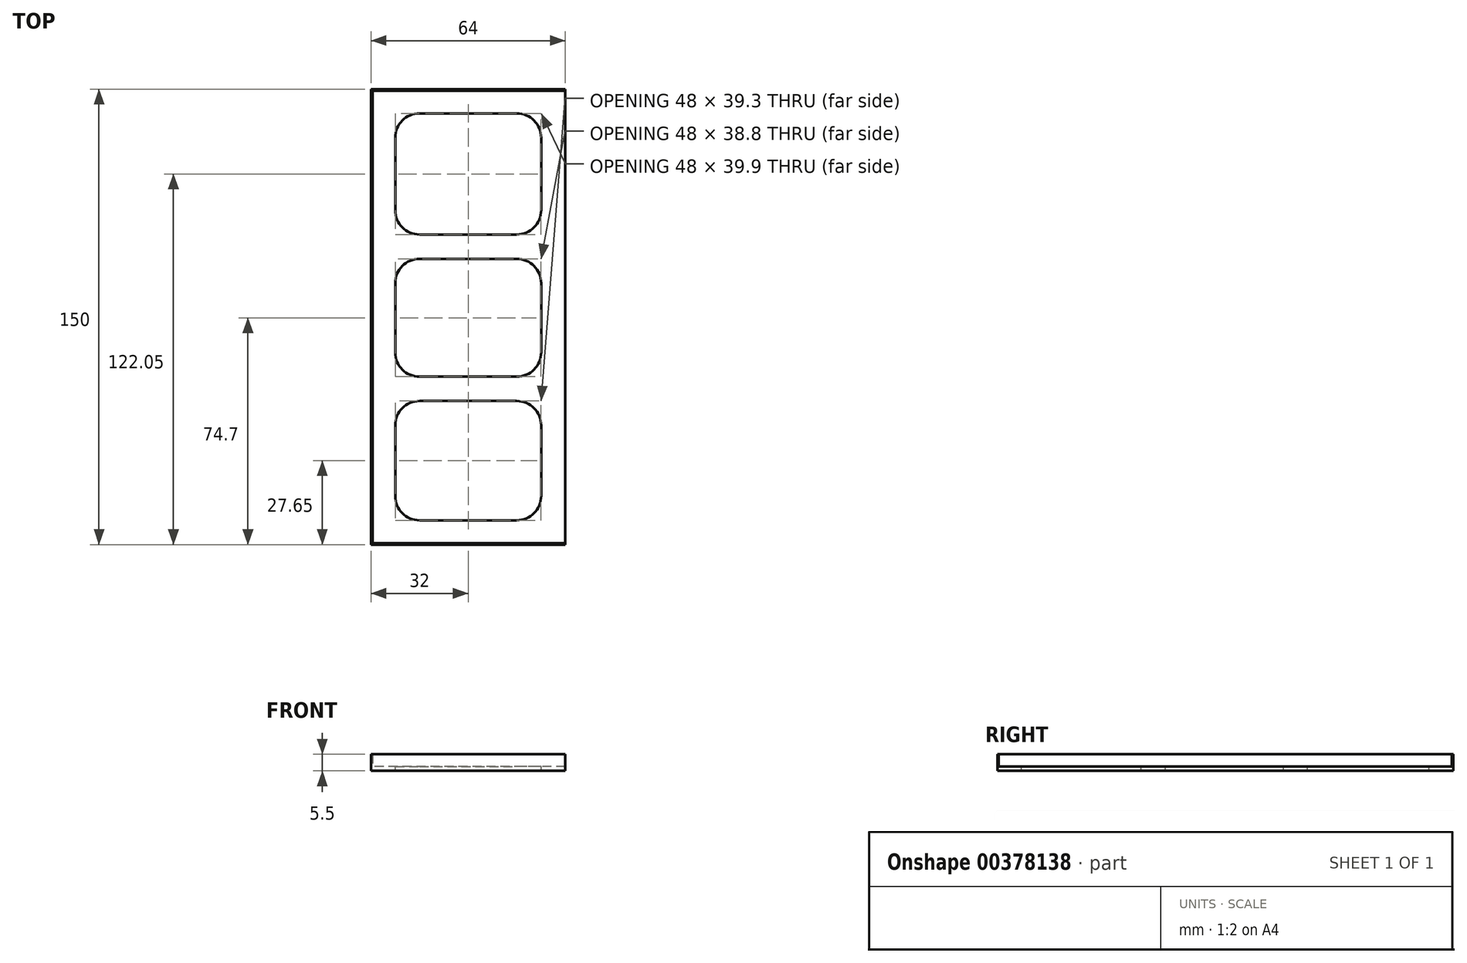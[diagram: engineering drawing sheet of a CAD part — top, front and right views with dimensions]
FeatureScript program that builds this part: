
annotation { "Feature Type Name" : "Feature", "Feature Type Description" : "" }
export const myFeature = defineFeature(function(context is Context, id is Id, definition is map)
    precondition{}
    {
        {
            var Q0;
            Q0=qCreatedBy(makeId("Top.planeOp"),FACE);
            var sketch = newSketch(context, id + "F0", { "sketchPlane" : qUnion([Q0])});
            skLineSegment(sketch, "E0.bottom", {"start": v(0, 0) * mm, "end": v(64, 0) * mm});
            skLineSegment(sketch, "E0.top", {"start": v(0, 150) * mm, "end": v(64, 150) * mm});
            skLineSegment(sketch, "E0.left", {"start": v(0, 0) * mm, "end": v(0, 150) * mm});
            skLineSegment(sketch, "E0.right", {"start": v(64, 0) * mm, "end": v(64, 150) * mm});
            skSolve(sketch);
        }
        {
            var Q0;
            Q0=qSketchRegion(id+"F0",true);
            extrude(context, id + "F1", {"entities" : qUnion([Q0]), "flatOperationType" : FlatOperationType.REMOVE, "offsetDistance" : 25 * mm, "depth" : 1.5 * mm, "domain" : OperationDomain.MODEL});
        }
        {
            var Q0;
            Q0=makeQuery(id+"F1.opExtrude","CAP_FACE",FACE,{"disambiguationData":[OSD([sQuery(id+"F0.wireOp",EDGE,"E0.bottom"),sQuery(id+"F0.wireOp",EDGE,"E0.top"),sQuery(id+"F0.wireOp",EDGE,"E0.left"),sQuery(id+"F0.wireOp",EDGE,"E0.right")])],"isStart":false});
            var sketch = newSketch(context, id + "F2", { "sketchPlane" : qUnion([Q0])});
            skLineSegment(sketch, "E1.bottom", {"start": v(8, 8) * mm, "end": v(56, 8) * mm});
            skLineSegment(sketch, "E1.top", {"start": v(8, 47.3) * mm, "end": v(56, 47.3) * mm});
            skLineSegment(sketch, "E1.left", {"start": v(8, 8) * mm, "end": v(8, 47.3) * mm});
            skLineSegment(sketch, "E1.right", {"start": v(56, 8) * mm, "end": v(56, 47.3) * mm});
            skLineSegment(sketch, "E2.bottom", {"start": v(8, 142) * mm, "end": v(56, 142) * mm});
            skLineSegment(sketch, "E2.top", {"start": v(8, 102.1) * mm, "end": v(56, 102.1) * mm});
            skLineSegment(sketch, "E2.left", {"start": v(8, 142) * mm, "end": v(8, 102.1) * mm});
            skLineSegment(sketch, "E2.right", {"start": v(56, 142) * mm, "end": v(56, 102.1) * mm});
            skLineSegment(sketch, "E3.bottom", {"start": v(8, 94.1) * mm, "end": v(56, 94.1) * mm});
            skLineSegment(sketch, "E3.top", {"start": v(8, 55.3) * mm, "end": v(56, 55.3) * mm});
            skLineSegment(sketch, "E3.left", {"start": v(8, 94.1) * mm, "end": v(8, 55.3) * mm});
            skLineSegment(sketch, "E3.right", {"start": v(56, 94.1) * mm, "end": v(56, 55.3) * mm});
            skSolve(sketch);
        }
        {
            var Q0;
            Q0=makeQuery(id+"F2.imprint","IMPRINT",FACE,{"disambiguationData":[TD([[makeQuery(id+"F2.imprint","IMPRINT",EDGE,{"derivedFrom":sQuery(id+"F2.wireOp",EDGE,"E2.bottom")}),-1.0]])]});
            var Q1;
            Q1=makeQuery(id+"F2.imprint","IMPRINT",FACE,{"disambiguationData":[TD([[makeQuery(id+"F2.imprint","IMPRINT",EDGE,{"derivedFrom":sQuery(id+"F2.wireOp",EDGE,"E3.bottom")}),-1.0]])]});
            var Q2;
            Q2=makeQuery(id+"F2.imprint","IMPRINT",FACE,{"disambiguationData":[TD([[makeQuery(id+"F2.imprint","IMPRINT",EDGE,{"derivedFrom":sQuery(id+"F2.wireOp",EDGE,"E1.bottom")}),1.0]])]});
            extrude(context, id + "F3", {"entities" : qUnion([Q0, Q1, Q2]), "operationType" : NewBodyOperationType.REMOVE, "flatOperationType" : FlatOperationType.REMOVE, "endBound" : BoundingType.THROUGH_ALL, "oppositeDirection" : true, "offsetDistance" : 25 * mm, "depth" : 25 * mm, "domain" : OperationDomain.MODEL});
        }
        {
            var Q0;
            Q0=makeQuery(id+"F3.boolean.opBoolean","COPY",EDGE,{"derivedFrom":makeQuery(id+"F3.opExtrude","SWEPT_EDGE",EDGE,{"disambiguationData":[OSD([sQuery(id+"F2.wireOp",EDGE,"E2.bottom"),sQuery(id+"F2.wireOp",EDGE,"E2.left")])]})});
            var Q1;
            Q1=makeQuery(id+"F3.boolean.opBoolean","COPY",EDGE,{"derivedFrom":makeQuery(id+"F3.opExtrude","SWEPT_EDGE",EDGE,{"disambiguationData":[OSD([sQuery(id+"F2.wireOp",EDGE,"E3.bottom"),sQuery(id+"F2.wireOp",EDGE,"E3.left")])]})});
            var Q2;
            Q2=makeQuery(id+"F3.boolean.opBoolean","COPY",EDGE,{"derivedFrom":makeQuery(id+"F3.opExtrude","SWEPT_EDGE",EDGE,{"disambiguationData":[OSD([sQuery(id+"F2.wireOp",EDGE,"E1.top"),sQuery(id+"F2.wireOp",EDGE,"E1.left")])]})});
            var Q3;
            Q3=makeQuery(id+"F3.boolean.opBoolean","COPY",EDGE,{"derivedFrom":makeQuery(id+"F3.opExtrude","SWEPT_EDGE",EDGE,{"disambiguationData":[OSD([sQuery(id+"F2.wireOp",EDGE,"E2.top"),sQuery(id+"F2.wireOp",EDGE,"E2.left")])]})});
            var Q4;
            Q4=makeQuery(id+"F3.boolean.opBoolean","COPY",EDGE,{"derivedFrom":makeQuery(id+"F3.opExtrude","SWEPT_EDGE",EDGE,{"disambiguationData":[OSD([sQuery(id+"F2.wireOp",EDGE,"E3.top"),sQuery(id+"F2.wireOp",EDGE,"E3.left")])]})});
            var Q5;
            Q5=makeQuery(id+"F3.boolean.opBoolean","COPY",EDGE,{"derivedFrom":makeQuery(id+"F3.opExtrude","SWEPT_EDGE",EDGE,{"disambiguationData":[OSD([sQuery(id+"F2.wireOp",EDGE,"E1.bottom"),sQuery(id+"F2.wireOp",EDGE,"E1.left")])]})});
            var Q6;
            Q6=makeQuery(id+"F3.boolean.opBoolean","COPY",EDGE,{"derivedFrom":makeQuery(id+"F3.opExtrude","SWEPT_EDGE",EDGE,{"disambiguationData":[OSD([sQuery(id+"F2.wireOp",EDGE,"E2.top"),sQuery(id+"F2.wireOp",EDGE,"E2.right")])]})});
            var Q7;
            Q7=makeQuery(id+"F3.boolean.opBoolean","COPY",EDGE,{"derivedFrom":makeQuery(id+"F3.opExtrude","SWEPT_EDGE",EDGE,{"disambiguationData":[OSD([sQuery(id+"F2.wireOp",EDGE,"E3.top"),sQuery(id+"F2.wireOp",EDGE,"E3.right")])]})});
            var Q8;
            Q8=makeQuery(id+"F3.boolean.opBoolean","COPY",EDGE,{"derivedFrom":makeQuery(id+"F3.opExtrude","SWEPT_EDGE",EDGE,{"disambiguationData":[OSD([sQuery(id+"F2.wireOp",EDGE,"E1.bottom"),sQuery(id+"F2.wireOp",EDGE,"E1.right")])]})});
            var Q9;
            Q9=makeQuery(id+"F3.boolean.opBoolean","COPY",EDGE,{"derivedFrom":makeQuery(id+"F3.opExtrude","SWEPT_EDGE",EDGE,{"disambiguationData":[OSD([sQuery(id+"F2.wireOp",EDGE,"E2.bottom"),sQuery(id+"F2.wireOp",EDGE,"E2.right")])]})});
            var Q10;
            Q10=makeQuery(id+"F3.boolean.opBoolean","COPY",EDGE,{"derivedFrom":makeQuery(id+"F3.opExtrude","SWEPT_EDGE",EDGE,{"disambiguationData":[OSD([sQuery(id+"F2.wireOp",EDGE,"E3.bottom"),sQuery(id+"F2.wireOp",EDGE,"E3.right")])]})});
            var Q11;
            Q11=makeQuery(id+"F3.boolean.opBoolean","COPY",EDGE,{"derivedFrom":makeQuery(id+"F3.opExtrude","SWEPT_EDGE",EDGE,{"disambiguationData":[OSD([sQuery(id+"F2.wireOp",EDGE,"E1.top"),sQuery(id+"F2.wireOp",EDGE,"E1.right")])]})});
            fillet(context, id + "F4", {"entities" : qUnion([Q0, Q1, Q2, Q3, Q4, Q5, Q6, Q7, Q8, Q9, Q10, Q11]), "radius" : 8 * mm, "tangentPropagation" : true, "defaultsChanged" : false, "allowEdgeOverflow" : false, "vertexSettings" : [], "filletType" : FilletType.EDGE});
        }
        {
            var Q0;
            Q0=makeQuery(id+"F1.opExtrude","CAP_FACE",FACE,{"disambiguationData":[OSD([sQuery(id+"F0.wireOp",EDGE,"E0.bottom"),sQuery(id+"F0.wireOp",EDGE,"E0.top"),sQuery(id+"F0.wireOp",EDGE,"E0.left"),sQuery(id+"F0.wireOp",EDGE,"E0.right")])],"isStart":false});
            var sketch = newSketch(context, id + "F5", { "sketchPlane" : qUnion([Q0])});
            skLineSegment(sketch, "E4", {"start": v(64, 0) * mm, "end": v(0, 0) * mm});
            skLineSegment(sketch, "E5", {"start": v(0, 0) * mm, "end": v(0, 150) * mm});
            skLineSegment(sketch, "E6", {"start": v(0, 150) * mm, "end": v(64, 150) * mm});
            skLineSegment(sketch, "E7", {"start": v(64, 150) * mm, "end": v(64, 149.5) * mm});
            skLineSegment(sketch, "E8", {"start": v(64, 149.5) * mm, "end": v(0.5, 149.5) * mm});
            skLineSegment(sketch, "E9", {"start": v(0.5, 149.5) * mm, "end": v(0.5, 0.5) * mm});
            skLineSegment(sketch, "E10", {"start": v(0.5, 0.5) * mm, "end": v(64, 0.5) * mm});
            skLineSegment(sketch, "E11", {"start": v(64, 0.5) * mm, "end": v(64, 0) * mm});
            skSolve(sketch);
        }
        {
            var Q0;
            Q0=qSketchRegion(id+"F5",true);
            extrude(context, id + "F6", {"entities" : qUnion([Q0]), "operationType" : NewBodyOperationType.ADD, "flatOperationType" : FlatOperationType.REMOVE, "offsetDistance" : 25 * mm, "depth" : 4 * mm, "domain" : OperationDomain.MODEL});
        }
    });
